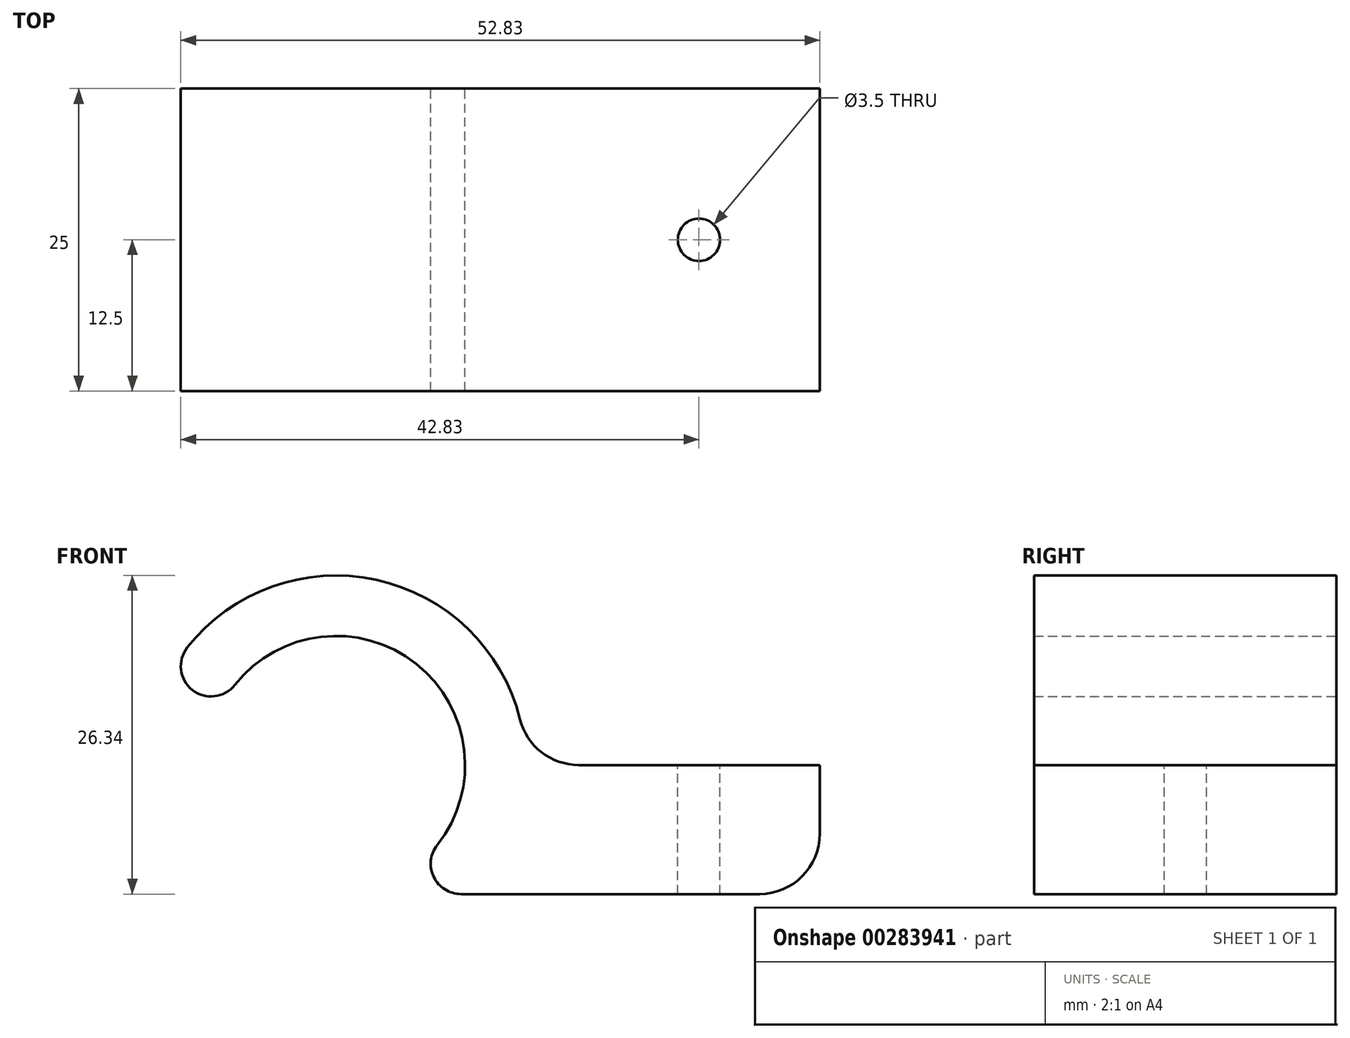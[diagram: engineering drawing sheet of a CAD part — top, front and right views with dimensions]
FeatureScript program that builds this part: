
annotation { "Feature Type Name" : "Feature", "Feature Type Description" : "" }
export const myFeature = defineFeature(function(context is Context, id is Id, definition is map)
    precondition{}
    {
        {
            var Q0;
            Q0=qCreatedBy(makeId("Front.planeOp"),FACE);
            var sketch = newSketch(context, id + "F0", { "sketchPlane" : qUnion([Q0])});
            skCircle(sketch, "E0", {"center": v(0, 0) * mm, "radius": 10.67 * mm, "construction": true});
            skLineSegment(sketch, "E1", {"start": v(0, 0) * mm, "end": v(52.75, 0) * mm, "construction": true});
            skArc(sketch, "E2", {"start": v(8.37, -6.62) * mm, "mid": v(6.62, 8.37) * mm, "end": v(-8.37, 6.62) * mm});
            skArc(sketch, "E3", {"start": v(-12.29, 9.72) * mm, "mid": v(-11.88, 6.2) * mm, "end": v(-8.37, 6.62) * mm});
            skArc(sketch, "E4", {"start": v(8.37, -6.62) * mm, "mid": v(8.08, -9.26) * mm, "end": v(10.33, -10.67) * mm});
            skLineSegment(sketch, "E5", {"start": v(0, 0) * mm, "end": v(0, -10.67) * mm, "construction": true});
            skLineSegment(sketch, "E6", {"start": v(0, -10.67) * mm, "end": v(62.64, -10.67) * mm, "construction": true});
            skCircle(sketch, "E7", {"center": v(0, 0) * mm, "radius": 15.67 * mm, "construction": true});
            skLineSegment(sketch, "E8", {"start": v(10.33, -8.17) * mm, "end": v(0, 0) * mm, "construction": true});
            skLineSegment(sketch, "E9", {"start": v(-10.33, 8.17) * mm, "end": v(0, 0) * mm, "construction": true});
            skLineSegment(sketch, "E10", {"start": v(40, 0) * mm, "end": v(40, -10.67) * mm});
            skLineSegment(sketch, "E11", {"start": v(40, -10.67) * mm, "end": v(10.33, -10.67) * mm});
            skArc(sketch, "E12", {"start": v(-12.29, 9.72) * mm, "mid": v(5.14, 14.8) * mm, "end": v(15.67, 0) * mm});
            skLineSegment(sketch, "E13", {"start": v(15.67, 0) * mm, "end": v(40, 0) * mm});
            skSolve(sketch);
        }
        {
            var Q0;
            Q0 = qSketchRegion(id + "F0", true);
            extrude(context, id + "F1", {"entities" : qUnion([Q0]), "endBound" : BoundingType.SYMMETRIC, "depth" : 25 * mm});
        }
        {
            var Q0;
            Q0=makeQuery(id+"F1.opExtrude","SWEPT_EDGE",EDGE,{"disambiguationData":[OSD([sQuery(id+"F0.wireOp",EDGE,"E12"),sQuery(id+"F0.wireOp",EDGE,"E13")])]});
            var Q1;
            Q1=makeQuery(id+"F1.opExtrude","SWEPT_EDGE",EDGE,{"disambiguationData":[OSD([sQuery(id+"F0.wireOp",EDGE,"E10"),sQuery(id+"F0.wireOp",EDGE,"E11")])]});
            fillet(context, id + "F2", {"entities" : qUnion([Q0, Q1]), "radius" : 5 * mm, "tangentPropagation" : true, "allowEdgeOverflow" : false});
        }
        {
            var Q0;
            Q0=qCreatedBy(makeId("Top.planeOp"),FACE);
            var sketch = newSketch(context, id + "F3", { "sketchPlane" : qUnion([Q0])});
            skLineSegment(sketch, "E14", {"start": v(0, 0) * mm, "end": v(30, 0) * mm, "construction": true});
            skCircle(sketch, "E15", {"center": v(30, 0) * mm, "radius": 1.75 * mm});
            skSolve(sketch);
        }
        {
            var Q0;
            Q0 = qSketchRegion(id + "F3", true);
            extrude(context, id + "F4", {"entities" : qUnion([Q0]), "operationType" : NewBodyOperationType.REMOVE, "endBound" : BoundingType.THROUGH_ALL, "oppositeDirection" : true, "depth" : 25 * mm});
        }
    });
